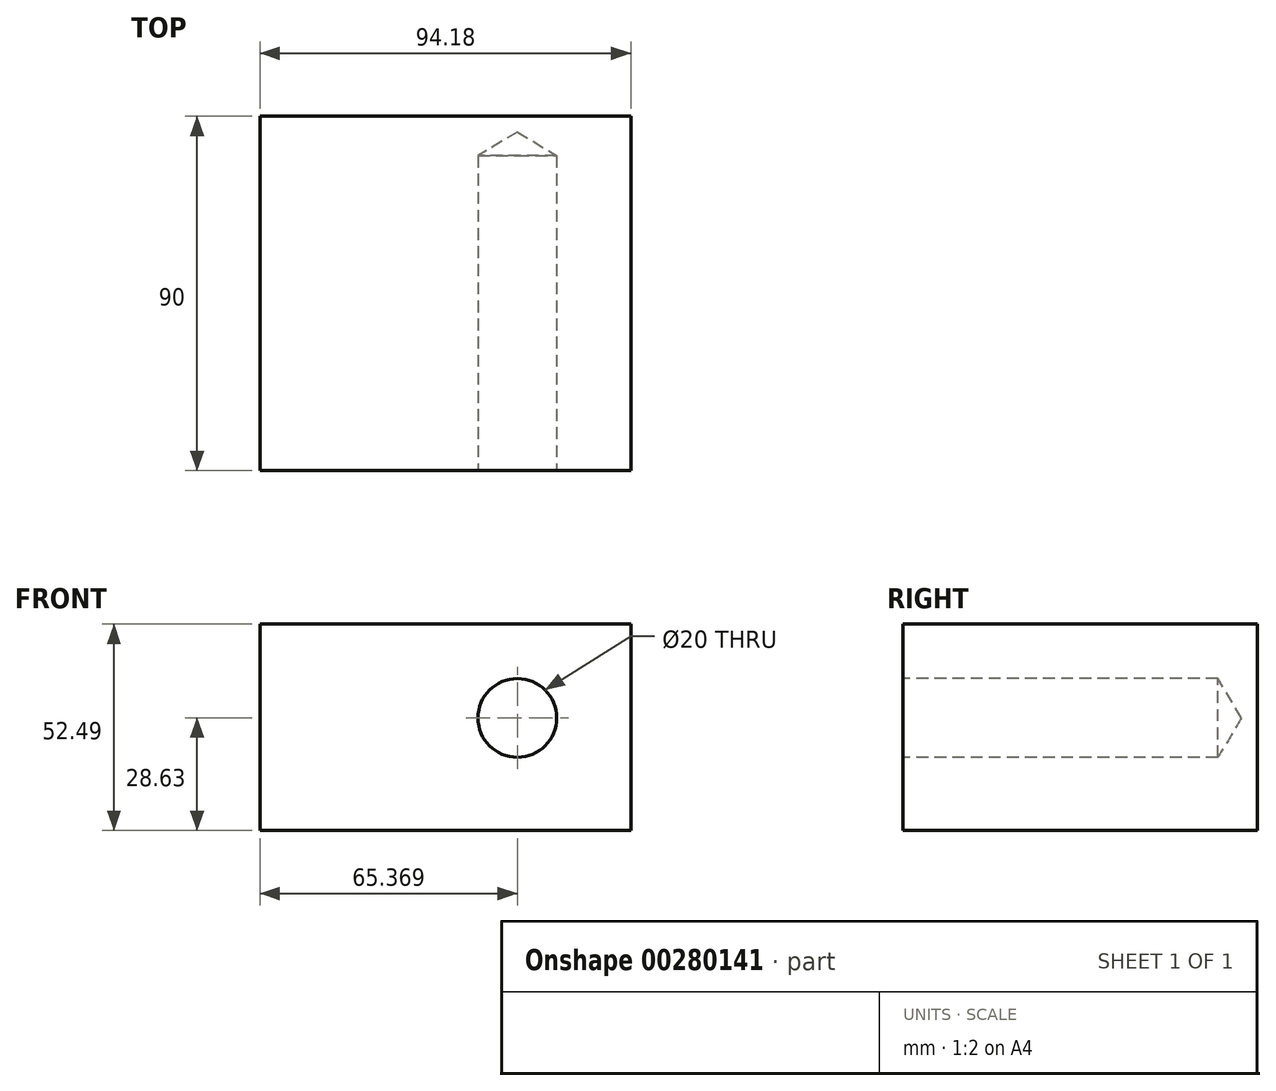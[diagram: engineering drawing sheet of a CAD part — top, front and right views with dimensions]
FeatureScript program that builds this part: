
annotation { "Feature Type Name" : "Feature", "Feature Type Description" : "" }
export const myFeature = defineFeature(function(context is Context, id is Id, definition is map)
    precondition{}
    {
        {
            var Q0;
            Q0=qCreatedBy(makeId("Front.planeOp"),FACE);
            var sketch = newSketch(context, id + "F0", { "sketchPlane" : qUnion([Q0])});
            skLineSegment(sketch, "E0.bottom", {"start": v(-37.13, 23.86) * mm, "end": v(57.05, 23.86) * mm});
            skLineSegment(sketch, "E0.top", {"start": v(-37.13, -28.63) * mm, "end": v(57.05, -28.63) * mm});
            skLineSegment(sketch, "E0.left", {"start": v(-37.13, 23.86) * mm, "end": v(-37.13, -28.63) * mm});
            skLineSegment(sketch, "E0.right", {"start": v(57.05, 23.86) * mm, "end": v(57.05, -28.63) * mm});
            skSolve(sketch);
        }
        {
            var Q0;
            Q0=makeQuery(id+"F0.imprint","IMPRINT",FACE,{"disambiguationData":[TD([[makeQuery(id+"F0.imprint","IMPRINT",EDGE,{"derivedFrom":sQuery(id+"F0.wireOp",EDGE,"E0.bottom")}),-1.0]])]});
            extrude(context, id + "F1", {"entities" : qUnion([Q0]), "depth" : 90 * mm});
        }
        {
            var Q0;
            Q0=makeQuery(id+"F1.opExtrude","CAP_FACE",FACE,{"disambiguationData":[OSD([sQuery(id+"F0.wireOp",EDGE,"E0.bottom"),sQuery(id+"F0.wireOp",EDGE,"E0.top"),sQuery(id+"F0.wireOp",EDGE,"E0.left"),sQuery(id+"F0.wireOp",EDGE,"E0.right")])],"isStart":false});
            var sketch = newSketch(context, id + "F2", { "sketchPlane" : qUnion([Q0])});
            skSolve(sketch);
        }
        {
            var Q0;
            Q0=makeQuery(id+"F2.imprint","IMPRINT",FACE,{"disambiguationData":[TD([[makeQuery(id+"F2.imprint","IMPRINT",EDGE,{"derivedFrom":makeQuery(id+"F1.opExtrude","CAP_EDGE",EDGE,{"disambiguationData":[OSD([sQuery(id+"F0.wireOp",EDGE,"E0.bottom")])],"isStart":false})}),-1.0]])]});
            var sketch = newSketch(context, id + "F3", { "sketchPlane" : qUnion([Q0])});
            skCircle(sketch, "E1", {"center": v(28.24, 0) * mm, "radius": 4.78 * mm});
            skSolve(sketch);
        }
        {
            var Q0;
            Q0=sQuery(id+"F3.wireOp",VERTEX,"E1.center");
            var Q1;
            Q1=makeQuery(id+"F1.opExtrude","SWEPT_BODY",BODY,{"disambiguationData":[OSD([sQuery(id+"F0.wireOp",EDGE,"E0.bottom"),sQuery(id+"F0.wireOp",EDGE,"E0.top"),sQuery(id+"F0.wireOp",EDGE,"E0.left"),sQuery(id+"F0.wireOp",EDGE,"E0.right")])]});
            hole(context, id + "F4", {"style" : HoleStyle.SIMPLE, "endStyle" : HoleEndStyle.BLIND, "holeDiameter" : 20 * mm, "holeDepth" : 80 * mm, "tappedDepth" : 12 * mm, "tapClearance" : 3, "locations" : qUnion([Q0]), "scope" : qUnion([Q1])});
        }
        {
            var Q0;
            Q0=makeQuery(id+"F2.imprint","IMPRINT",FACE,{"disambiguationData":[TD([[makeQuery(id+"F2.imprint","IMPRINT",EDGE,{"derivedFrom":makeQuery(id+"F1.opExtrude","CAP_EDGE",EDGE,{"disambiguationData":[OSD([sQuery(id+"F0.wireOp",EDGE,"E0.bottom")])],"isStart":false})}),-1.0]])]});
            var sketch = newSketch(context, id + "F5", { "sketchPlane" : qUnion([Q0])});
            skCircle(sketch, "E2", {"center": v(-17.23, 0) * mm, "radius": 9.11 * mm});
            skSolve(sketch);
        }
        {
            var Q0;
            Q0=sQuery(id+"F5.wireOp",EDGE,"E2");
            extrude(context, id + "F6", {"bodyType" : ToolBodyType.SURFACE, "surfaceEntities" : qUnion([Q0]), "depth" : 80 * mm});
        }
        {
            var Q0;
            Q0=makeQuery(id+"F5.imprint","IMPRINT",FACE,{"disambiguationData":[TD([[makeQuery(id+"F5.imprint","IMPRINT",EDGE,{"derivedFrom":sQuery(id+"F5.wireOp",EDGE,"E2")}),1.0]])]});
            extrude(context, id + "F7", {"entities" : qUnion([Q0]), "operationType" : NewBodyOperationType.REMOVE, "depth" : 80 * mm});
        }
    });
